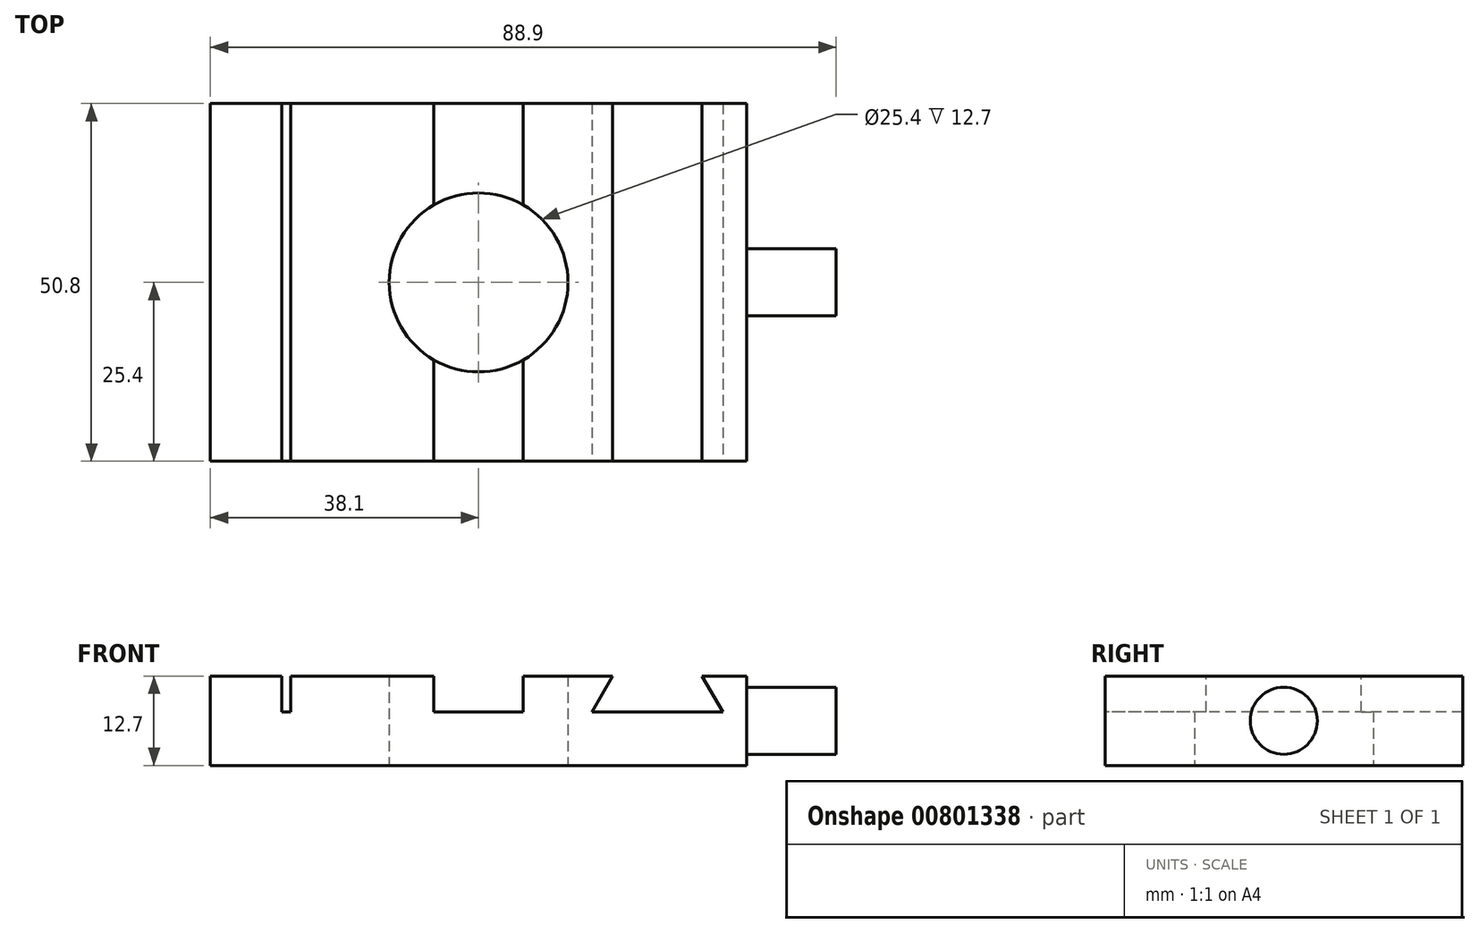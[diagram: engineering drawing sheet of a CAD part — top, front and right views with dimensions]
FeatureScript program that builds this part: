
annotation { "Feature Type Name" : "Feature", "Feature Type Description" : "" }
export const myFeature = defineFeature(function(context is Context, id is Id, definition is map)
    precondition{}
    {
        {
            var Q0;
            Q0=qCreatedBy(makeId("Top.planeOp"),FACE);
            var sketch = newSketch(context, id + "F0", { "sketchPlane" : qUnion([Q0])});
            skLineSegment(sketch, "E0.bottom", {"start": v(38.1, -25.4) * mm, "end": v(-38.1, -25.4) * mm});
            skLineSegment(sketch, "E0.top", {"start": v(38.1, 25.4) * mm, "end": v(-38.1, 25.4) * mm});
            skLineSegment(sketch, "E0.left", {"start": v(38.1, -25.4) * mm, "end": v(38.1, 25.4) * mm});
            skLineSegment(sketch, "E0.right", {"start": v(-38.1, -25.4) * mm, "end": v(-38.1, 25.4) * mm});
            skPoint(sketch, "E0.middle", {"position": v(0, 0) * mm});
            skCircle(sketch, "E1", {"center": v(0, 0) * mm, "radius": 12.7 * mm});
            skSolve(sketch);
        }
        {
            var Q0;
            Q0 = qSketchRegion(id + "F0", true);
            extrude(context, id + "F1", {"entities" : qUnion([Q0]), "depth" : 12.7 * mm, "offsetDistance" : 25.4 * mm});
        }
        {
            var Q0;
            Q0=makeQuery(id+"F1.opExtrude","CAP_FACE",FACE,{"disambiguationData":[OSD([sQuery(id+"F0.wireOp",EDGE,"E0.bottom"),sQuery(id+"F0.wireOp",EDGE,"E0.top"),sQuery(id+"F0.wireOp",EDGE,"E0.left"),sQuery(id+"F0.wireOp",EDGE,"E0.right"),sQuery(id+"F0.wireOp",EDGE,"E1")])],"isStart":false});
            var sketch = newSketch(context, id + "F2", { "sketchPlane" : qUnion([Q0])});
            skLineSegment(sketch, "E2.bottom", {"start": v(-27.94, 25.4) * mm, "end": v(-26.67, 25.4) * mm});
            skLineSegment(sketch, "E2.top", {"start": v(-27.94, -25.4) * mm, "end": v(-26.67, -25.4) * mm});
            skLineSegment(sketch, "E2.left", {"start": v(-27.94, 25.4) * mm, "end": v(-27.94, -25.4) * mm});
            skLineSegment(sketch, "E2.right", {"start": v(-26.67, 25.4) * mm, "end": v(-26.67, -25.4) * mm});
            skLineSegment(sketch, "E3", {"start": v(-6.35, 25.4) * mm, "end": v(-6.35, -25.4) * mm});
            skLineSegment(sketch, "E4", {"start": v(-6.35, -25.4) * mm, "end": v(6.35, -25.4) * mm});
            skLineSegment(sketch, "E5", {"start": v(6.35, -25.4) * mm, "end": v(6.35, 25.4) * mm});
            skLineSegment(sketch, "E6", {"start": v(6.35, 25.4) * mm, "end": v(-6.35, 25.4) * mm});
            skPoint(sketch, "E7", {"position": v(0, 0) * mm});
            skLineSegment(sketch, "E8", {"start": v(0, 25.4) * mm, "end": v(0, -25.4) * mm, "construction": true});
            skSolve(sketch);
        }
        {
            var Q0;
            Q0=makeQuery(id+"F2.imprint","IMPRINT",FACE,{"disambiguationData":[TD([[makeQuery(id+"F2.imprint","IMPRINT",EDGE,{"derivedFrom":sQuery(id+"F2.wireOp",EDGE,"E2.bottom")}),1.0]])]});
            var Q1;
            {var subQ0=sQuery(id+"F2.wireOp",EDGE,"E6");Q1=makeQuery(id+"F2.imprint","IMPRINT",FACE,{"disambiguationData":[TD([[makeQuery(id+"F2.imprint","IMPRINT",EDGE,{"derivedFrom":subQ0}),1.0]])]});}
            var Q2;
            {var subQ0=sQuery(id+"F2.wireOp",EDGE,"E4");Q2=makeQuery(id+"F2.imprint","IMPRINT",FACE,{"disambiguationData":[TD([[makeQuery(id+"F2.imprint","IMPRINT",EDGE,{"derivedFrom":subQ0}),-1.0]])]});}
            extrude(context, id + "F3", {"entities" : qUnion([Q0, Q1, Q2]), "operationType" : NewBodyOperationType.REMOVE, "oppositeDirection" : true, "depth" : 5.08 * mm, "offsetDistance" : 25.4 * mm});
        }
        {
            var Q0;
            Q0=makeQuery(id+"F1.opExtrude","SWEPT_FACE",FACE,{"disambiguationData":[OSD([sQuery(id+"F0.wireOp",EDGE,"E0.bottom")])]});
            var sketch = newSketch(context, id + "F4", { "sketchPlane" : qUnion([Q0])});
            skLineSegment(sketch, "E9", {"start": v(19.05, 12.7) * mm, "end": v(16.12, 7.62) * mm});
            skLineSegment(sketch, "E10", {"start": v(16.12, 7.62) * mm, "end": v(34.68, 7.62) * mm});
            skLineSegment(sketch, "E11", {"start": v(34.68, 7.62) * mm, "end": v(31.75, 12.7) * mm});
            skLineSegment(sketch, "E12", {"start": v(31.75, 12.7) * mm, "end": v(19.05, 12.7) * mm});
            skLineSegment(sketch, "E13", {"start": v(25.4, 7.62) * mm, "end": v(25.4, 12.7) * mm, "construction": true});
            skSolve(sketch);
        }
        {
            var Q0;
            Q0=makeQuery(id+"F4.imprint","IMPRINT",FACE,{"disambiguationData":[TD([[makeQuery(id+"F4.imprint","IMPRINT",EDGE,{"derivedFrom":sQuery(id+"F4.wireOp",EDGE,"E9")}),1.0]])]});
            extrude(context, id + "F5", {"entities" : qUnion([Q0]), "operationType" : NewBodyOperationType.REMOVE, "endBound" : BoundingType.THROUGH_ALL, "oppositeDirection" : true, "depth" : 25.4 * mm, "offsetDistance" : 25.4 * mm});
        }
        {
            var Q0;
            Q0=makeQuery(id+"F1.opExtrude","SWEPT_FACE",FACE,{"disambiguationData":[OSD([sQuery(id+"F0.wireOp",EDGE,"E0.left")])]});
            var sketch = newSketch(context, id + "F6", { "sketchPlane" : qUnion([Q0])});
            skCircle(sketch, "E14", {"center": v(0, 6.35) * mm, "radius": 4.76 * mm});
            skPoint(sketch, "E14.centerSnap0", {"position": v(-25.4, 6.35) * mm});
            skPoint(sketch, "E14.centerSnap1", {"position": v(0, 12.7) * mm});
            skSolve(sketch);
        }
        {
            var Q0;
            Q0=makeQuery(id+"F6.imprint","IMPRINT",FACE,{"disambiguationData":[TD([[makeQuery(id+"F6.imprint","IMPRINT",EDGE,{"derivedFrom":sQuery(id+"F6.wireOp",EDGE,"E14")}),1.0]])]});
            extrude(context, id + "F7", {"entities" : qUnion([Q0]), "operationType" : NewBodyOperationType.ADD, "depth" : 12.7 * mm, "offsetDistance" : 25.4 * mm});
        }
    });
